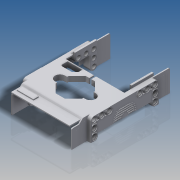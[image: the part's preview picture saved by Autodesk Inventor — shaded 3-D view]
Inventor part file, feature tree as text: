
AUTODESK INVENTOR PART (.ipt)
format: ipt  version: 2016 SP2 (Build 200236200, 236)  size: 1,872,384 bytes
history: native  units: in
note: dims shown in document units (in); Inventor stores cm internally (conversion verified against a paired STEP export)
features: extrude x21, sketch x12, plane x4, projected_geometry x4, fillet x2, mirror x1
ambient origin geometry x8: Origin, YZ Plane, XZ Plane, XY Plane, X Axis, Y Axis, Z Axis, Center Point
bodies: Solid1 (feature_tree)
feature tree (44):
  sketch  "Sketch2"  dims[d1=0.4157in d2=1.2441in d3=1.0866in]
  extrude  "Extrusion1"  Depth=1.2441in
  extrude  "Extrusion2"  Depth=1.2598in
  extrude  "Extrusion3"  Depth=0.0346in
  extrude  "Extrusion10"  Depth=2.5197in
  fillet  "Fillet1"  Radius=2.5197in
  sketch  "Sketch3"  dims[d4=0.378in d5=1.2598in]
  extrude  "Extrusion4"  Depth=0.0787in
  extrude  "Extrusion5"  Depth=1.8425in
  extrude  "Extrusion6"  Depth=1.2441in
  extrude  "Extrusion7"  Depth=0.9449in
  sketch  "Sketch4"  dims[d6=0.0346in d7=0.0346in]
  extrude  "Extrusion8"  Depth=0.2205in TaperAngle=0.0deg
  extrude  "Extrusion9"  Depth=0.9134in
  extrude  "Extrusion13"  Depth=0.1433in
  mirror  "Mirror1"
  plane  "Work Plane1"
  sketch  "Sketch6"  dims[d11=0.0472in d12=0.0787in]
  extrude  "Extrusion11"  Depth=0.0472in
  extrude  "Extrusion12"  Depth=0.0472in
  plane  "Work Plane2"
  sketch  "Sketch7"  dims[d13=0.8189in d14=1.8425in d15=2.2205in d16=1.8425in]
  extrude  "Extrusion14"  Depth=0.0472in
  extrude  "Extrusion19"  Depth=0.0472in
  extrude  "Extrusion15"  Depth=0.0315in
  extrude  "Extrusion20"  Depth=0.0315in
  extrude  "Extrusion21"  Depth=0.0315in
  plane  "Work Plane3"
  extrude  "Extrusion16"  Depth=0.0472in
  extrude  "Extrusion17"  Depth=0.2835in
  plane  "Work Plane4"
  extrude  "Extrusion18"  Depth=0.0472in
  fillet  "Fillet2"  Radius=0.315in
  projected_geometry  "Projected Loop1"
  sketch  "Sketch5"  dims[d8=0.0346in d9=0.4315in d10=2.5197in]
  sketch  "Sketch8"  dims[d17=2.2205in d18=1.2441in]
  projected_geometry  "Projected Loop2"
  sketch  "Sketch9"  dims[d19=0.8189in d20=0.9449in]
  sketch  "Sketch10"  dims[d21=0.0472in d22=0.0in d23=0.2205in d24=0.0in]
  sketch  "Sketch11"  dims[d25=0.9134in d26=0.0in d27=0.2929in]
  sketch  "Sketch12"  dims[d28=0.6016in d29=0.1433in]
  projected_geometry  "Projected Loop3"
  sketch  "Sketch13"  dims[d30=0.1433in d31=0.063in d32=0.4866in d33=0.0472in d34=0.0445in d35=0.0315in d36=0.0315in d37=0.0315in d38=0.0472in d39=0.2835in d40=0.189in d41=0.315in d42=0.6299in d43=0.1102in d44=0.0787in d45=0.0in d46=0.2047in d47=0.0in d48=0.2047in d49=0.0in d50=0.6299in d51=0.2047in d52=0.0in d53=0.2441in d54=45.0deg d55=0.252in d56=0.0in d57=0.0315in d58=0.0in d59=0.2992in d60=0.4567in d61=0.1575in d62=0.0315in d63=0.0in d64=0.1496in d65=0.2362in d66=0.5669in d67=0.2047in d68=0.4094in d69=0.2205in d70=0.0787in d71=0.5669in d72=0.1069in d73=0.3465in d74=0.0315in d75=0.0in d76=0.0394in d77=0.0in d78=0.1496in d79=0.4094in d80=0.9622in d81=0.298in d82=0.3236in d83=0.8118in d84=0.0358in d85=0.4063in d86=0.0394in d87=0.022in d88=0.0394in d89=0.022in d90=0.0772in d91=0.0394in d92=0.022in d93=0.0772in d94=0.0394in d95=0.0772in d96=0.022in d97=0.1417in d98=0.1339in d99=0.1417in d100=0.1417in d101=0.0079in d102=0.0in d104=0.9618in d105=0.8118in d106=0.022in d107=0.0394in d108=0.0772in d109=0.0772in d111=0.298in d112=0.3236in d113=0.0394in d114=0.0in d115=0.0079in d116=0.0in d117=0.0079in d118=0.0315in d119=0.3465in d120=0.0in d122=0.0472in d123=0.3465in d124=0.0in d125=-0.0063in d126=0.1575in d127=0.685in d128=0.2206in d129=0.0866in d130=0.3465in d131=0.0in d135=0.3465in d136=0.0in d137=1.126in d138=0.0039in d139=0.0157in d140=0.3465in d141=0.0in d142=0.3465in d143=0.0in d144=0.0472in d145=0.0472in d146=0.0472in]
  projected_geometry  "Projected Loop4"
